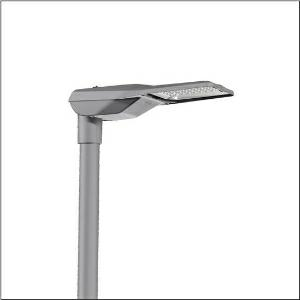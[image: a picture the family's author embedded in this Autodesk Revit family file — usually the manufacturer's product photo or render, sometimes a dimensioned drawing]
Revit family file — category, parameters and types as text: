
# Revit family: streetlight_sl_21_iq_mini___p0_5a_5xe2v31v08gb_1d9f
name_source: partatom
category: Lighting Fixtures
units: mm (PartAtom-declared; Revit-internal decimal feet)

## family parameters
Cut with Voids When Loaded = No
Host = Face
Light Source = No
Part Type = Normal
Room Calculation Point = No
Round Connector Dimension = Use Diameter
Shared = No

## types (1)
- --- (1 x LED, 5880 lm, 39.8 W, 3000K)
    Apparent Load = 40 VA
    CIE Flux Codes = 37 73 96 100 100
    Color Rendering = 70
    Color Temperature = 3000K
    Default Elevation = 1800 mm
    Description = Streetlight SL 21 iQ mini, mast luminaire, primary light control with lens, of PMMA, primary optical cover: cover, of toughened safety glass, transparent, light distribution: P0.5a, light emission: direct distribution, primary light characteristic: asymmetric, installation type: post-top, side-entry, LED, High Power LED, rated luminous flux: 5.880lm, luminous efficacy: 148lm/W, light colour: 730, colour temperature: 3000K, control gear: iQ-Street Remote, D4i with power reduction, control: pre-setting: logarithmic dimming characteristic, Street-Remote, Auto-Match, Temp-Guard, Lumen-Switch, Night-Set, Smart-Wire, Light-Fading, Desk-Remote (wireless, voltage-free reading and setting of iQ features in the workshop via application-optimized NFC function/RFID function), optimised constant luminous flux control (CLO 2.0), mains connection: 220..240V, AC, 50/60Hz, start of lifetime: 40W, end of service life: 41W, reduction: 18W, luminaire housing, of diecast aluminium, powder-coated, SITECO metallic grey (DB 702S), corrosivity category C5 high according to DIN EN ISO 12944, please order mast flange separately, inclination adjustable: 0°, 5°, 10°, 15°, sealing non-destructively replaceable, multi-level sealing system, length: 628mm, width: 235mm, height: 110mm, mast flange for spigot size: 42mm (side-entry): 5XC10008XM4, 60/48mm (side-entry/post-top): 5XC10108XM2, 76/60mm (side-entry/post-top): 5XC10108XM1, mounting height: 4..8m, Smart Interface above, protection rating (complete): IP66, insulation class (complete): insulation class II (safety insulation), certification: CE, ENEC, ENEC+, VDE, impact resistance: IK10, permissible operating ambient temperature for outdoor applications: -40..+50°C, standard-compliant lighting for roads and squares, packaging unit: 1 piece

Light Distribution: P0.5a
    Height = 110 mm
    Lamp = 1 x LED
    Lamp Light Flux = 5880 lm
    Lamp Power = 39.8 W
    Lamp count = 1
    Length = 625 mm
    Luminous efficacy = 148 lm/W
    Manufacturer = Siteco
    ModVariant = No
    Model = 5XE2V31V08GB
    Number of Poles = 1
    OnlyDefault = Yes
    Power Factor = 1
    Product Name = Streetlight SL 21 iQ mini | P0.5a
    Product group = mast luminaire | pylon top
    ProductGroupID = 6100
    Protection Class = Protection class II
    Protection Degree = IP 66
    RLX_Detail_Level = 1
    RLX_Emergency_Light_Flux = 0 lm
    RLX_Emergency_Type = 0
    RLX_Emergency_Type_DB = No
    RlxData = <blob elided: 92101 chars, md5=89016dd6>
    Socket = socket
    Standby Power = 0 W
    System Light Flux = 5880 lm
    System Power = 40 W
    Type Comments = factory setting: luminous flux: 100 % | dim-lin: 254 | 800 mA
    Type Image = l_1003515.jpg
    URL = http://relux.com
    VarID = @adj_078413
    Voltage = 0 V
    Weight = 0.00 kg
    Width = 234 mm

## geometry (parser evidence)
native form markers: Blend x4, Sweep x10
no freeform markers — native parametric forms only
